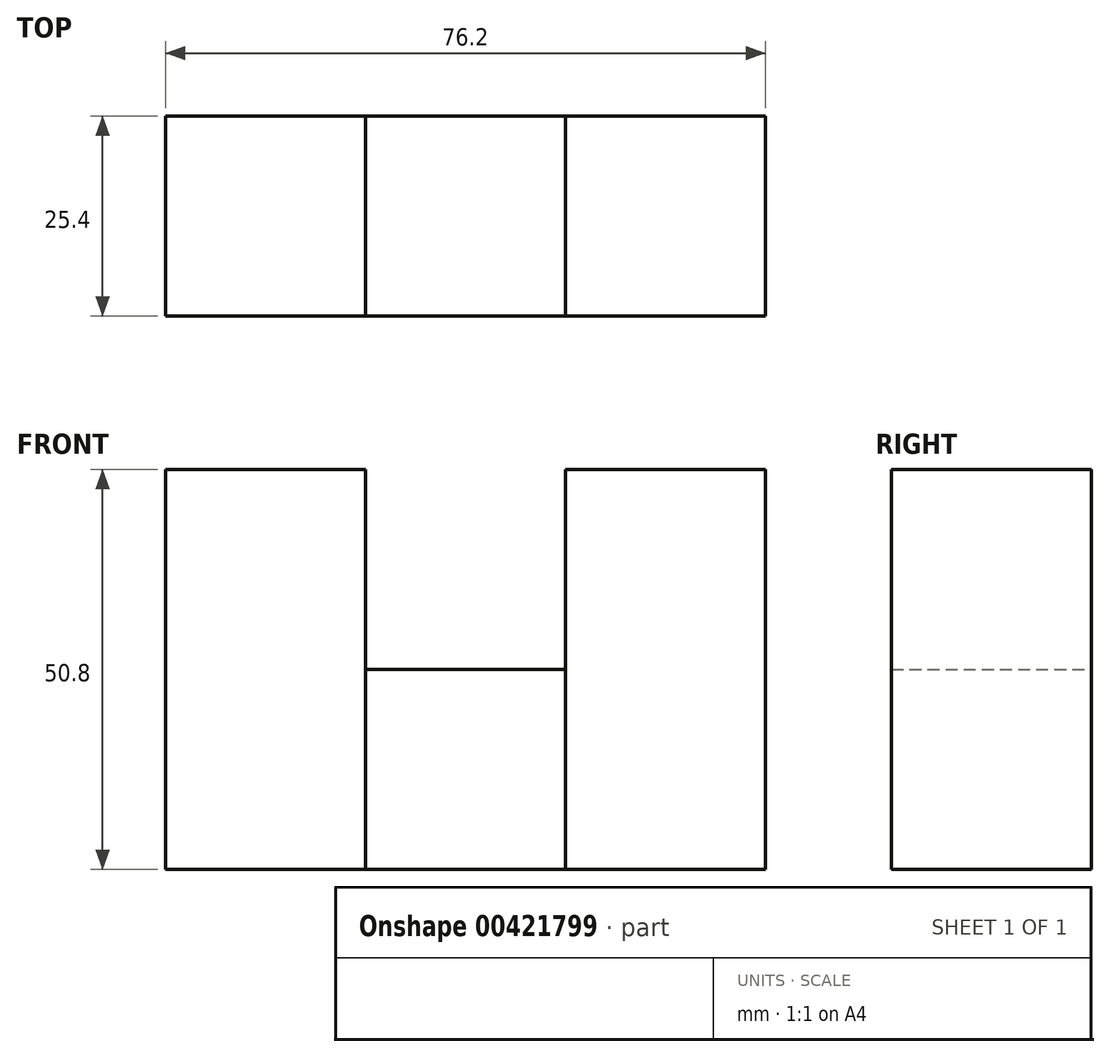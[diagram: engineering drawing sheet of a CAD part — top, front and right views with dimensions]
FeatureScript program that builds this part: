
annotation { "Feature Type Name" : "Feature", "Feature Type Description" : "" }
export const myFeature = defineFeature(function(context is Context, id is Id, definition is map)
    precondition{}
    {
        {
            var Q0;
            Q0=qCreatedBy(makeId("Front.planeOp"),FACE);
            var sketch = newSketch(context, id + "F0", { "sketchPlane" : qUnion([Q0])});
            skPoint(sketch, "E0.end.orphan", {"position": v(-25.4, 0) * mm});
            skPoint(sketch, "E1.orphan", {"position": v(-50.8, 0) * mm});
            skPoint(sketch, "E2.start.orphan", {"position": v(0, 0) * mm});
            skLineSegment(sketch, "E3", {"start": v(0, 0) * mm, "end": v(-76.2, 0) * mm});
            skLineSegment(sketch, "E4", {"start": v(-76.2, 0) * mm, "end": v(-76.2, 50.8) * mm});
            skLineSegment(sketch, "E5", {"start": v(-76.2, 50.8) * mm, "end": v(-50.8, 50.8) * mm});
            skLineSegment(sketch, "E6", {"start": v(-50.8, 50.8) * mm, "end": v(-50.8, 0) * mm});
            skLineSegment(sketch, "E7", {"start": v(0, 0) * mm, "end": v(0, 50.8) * mm});
            skLineSegment(sketch, "E8", {"start": v(0, 50.8) * mm, "end": v(-25.4, 50.8) * mm});
            skLineSegment(sketch, "E9", {"start": v(-25.4, 50.8) * mm, "end": v(-25.4, 0) * mm});
            skSolve(sketch);
        }
        {
            var Q0;
            Q0=qCreatedBy(makeId("Front.planeOp"),FACE);
            var sketch = newSketch(context, id + "F1", { "sketchPlane" : qUnion([Q0])});
            skLineSegment(sketch, "E10", {"start": v(-50.8, 0) * mm, "end": v(-50.8, 25.4) * mm});
            skLineSegment(sketch, "E11", {"start": v(-50.8, 25.4) * mm, "end": v(-25.4, 25.4) * mm});
            skLineSegment(sketch, "E12", {"start": v(-25.4, 25.4) * mm, "end": v(-25.4, 0) * mm});
            skLineSegment(sketch, "E13", {"start": v(-25.4, 0) * mm, "end": v(-50.8, 0) * mm});
            skSolve(sketch);
        }
        {
            var Q0;
            Q0 = qSketchRegion(id + "F1", true);
            var Q1;
            {var subQ0=sQuery(id+"F0.wireOp",EDGE,"E4");Q1=makeQuery(id+"F0.imprint","IMPRINT",FACE,{"disambiguationData":[TD([[makeQuery(id+"F0.imprint","IMPRINT",EDGE,{"derivedFrom":subQ0}),-1.0]])]});}
            var Q2;
            {var subQ0=sQuery(id+"F0.wireOp",EDGE,"E7");Q2=makeQuery(id+"F0.imprint","IMPRINT",FACE,{"disambiguationData":[TD([[makeQuery(id+"F0.imprint","IMPRINT",EDGE,{"derivedFrom":subQ0}),1.0]])]});}
            extrude(context, id + "F2", {"entities" : qUnion([Q0, Q1, Q2]), "depth" : 25.4 * mm});
        }
    });
